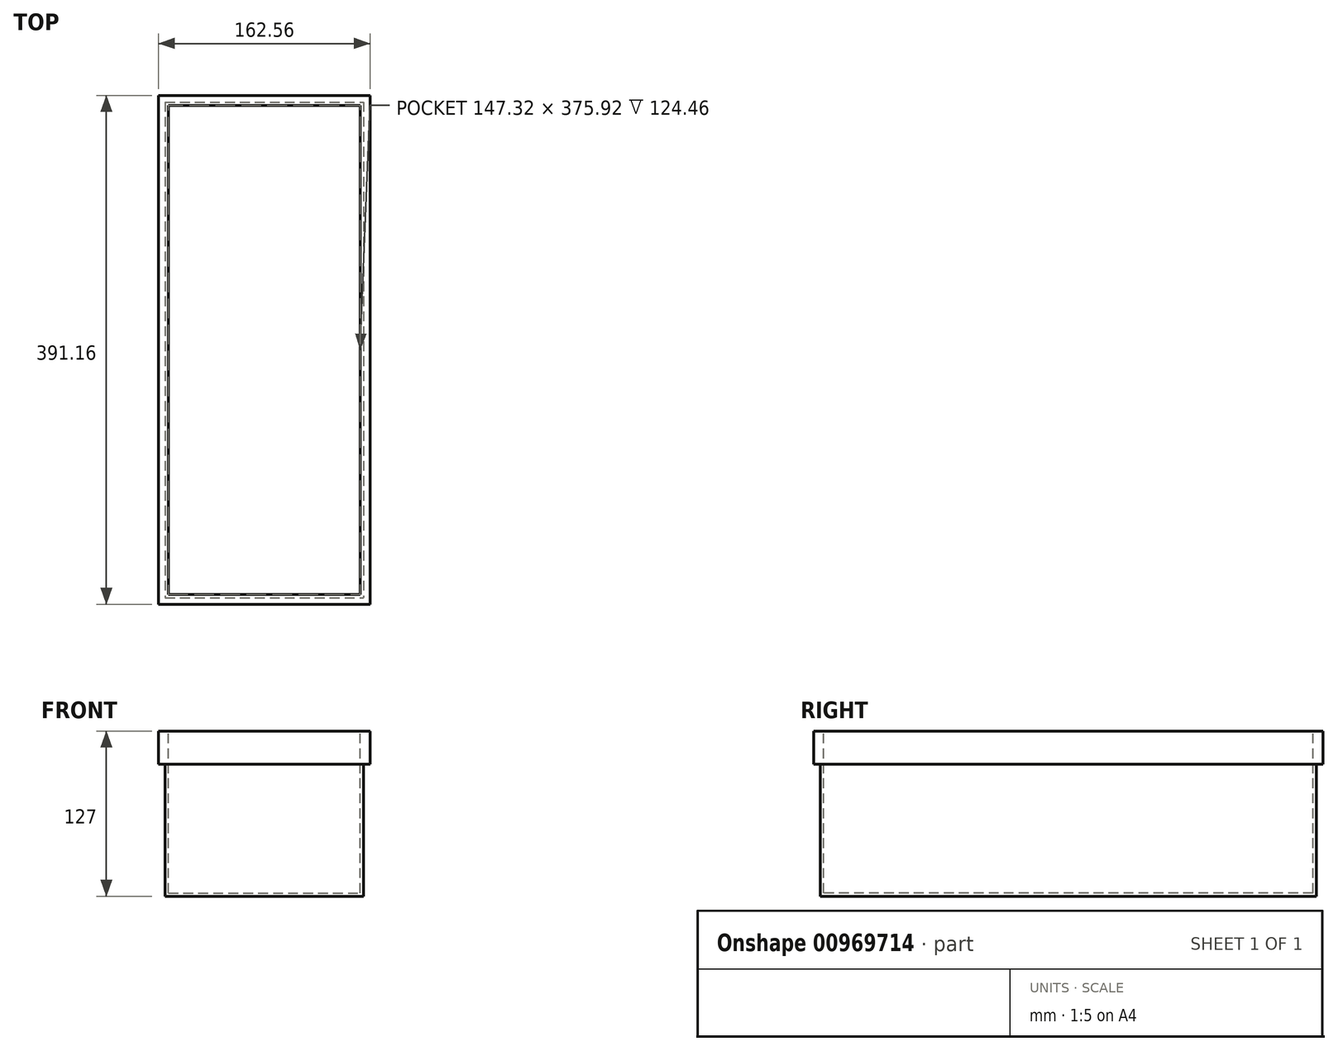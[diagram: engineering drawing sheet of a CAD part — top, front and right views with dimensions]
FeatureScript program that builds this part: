
annotation { "Feature Type Name" : "Feature", "Feature Type Description" : "" }
export const myFeature = defineFeature(function(context is Context, id is Id, definition is map)
    precondition{}
    {
        {
            var Q0;
            Q0=qCreatedBy(makeId("Front.planeOp"),FACE);
            var sketch = newSketch(context, id + "F0", { "sketchPlane" : qUnion([Q0])});
            skLineSegment(sketch, "E0.bottom", {"start": v(0, 0) * mm, "end": v(152.4, 0) * mm});
            skLineSegment(sketch, "E0.top", {"start": v(0, 127) * mm, "end": v(152.4, 127) * mm});
            skLineSegment(sketch, "E0.left", {"start": v(0, 0) * mm, "end": v(0, 127) * mm});
            skLineSegment(sketch, "E0.right", {"start": v(152.4, 0) * mm, "end": v(152.4, 127) * mm});
            skSolve(sketch);
        }
        {
            var Q0;
            Q0=makeQuery(id+"F0.imprint","IMPRINT",FACE,{"disambiguationData":[TD([[makeQuery(id+"F0.imprint","IMPRINT",EDGE,{"derivedFrom":sQuery(id+"F0.wireOp",EDGE,"E0.bottom")}),1.0]])]});
            extrude(context, id + "F1", {"entities" : qUnion([Q0]), "oppositeDirection" : true, "depth" : 381 * mm, "offsetDistance" : 25.4 * mm});
        }
        {
            var Q0;
            Q0=makeQuery(id+"F1.opExtrude","SWEPT_FACE",FACE,{"disambiguationData":[OSD([sQuery(id+"F0.wireOp",EDGE,"E0.top")])]});
            shell(context, id + "F2", {"entities" : qUnion([Q0]), "thickness" : 2.54 * mm});
        }
        {
            var Q0;
            Q0=makeQuery(id+"F1.opExtrude","SWEPT_FACE",FACE,{"disambiguationData":[OSD([sQuery(id+"F0.wireOp",EDGE,"E0.top")])]});
            var sketch = newSketch(context, id + "F3", { "sketchPlane" : qUnion([Q0])});
            skLineSegment(sketch, "E1.bottom", {"start": v(157.48, -5.08) * mm, "end": v(-5.08, -5.08) * mm});
            skLineSegment(sketch, "E1.top", {"start": v(157.48, 386.08) * mm, "end": v(-5.08, 386.08) * mm});
            skLineSegment(sketch, "E1.left", {"start": v(157.48, -5.08) * mm, "end": v(157.48, 386.08) * mm});
            skLineSegment(sketch, "E1.right", {"start": v(-5.08, -5.08) * mm, "end": v(-5.08, 386.08) * mm});
            skSolve(sketch);
        }
        {
            var Q0;
            Q0=makeQuery(id+"F3.imprint","IMPRINT",FACE,{"disambiguationData":[TD([[makeQuery(id+"F3.imprint","IMPRINT",EDGE,{"derivedFrom":sQuery(id+"F3.wireOp",EDGE,"E1.bottom")}),-1.0]])]});
            extrude(context, id + "F4", {"entities" : qUnion([Q0]), "operationType" : NewBodyOperationType.ADD, "oppositeDirection" : true, "depth" : 25.4 * mm, "offsetDistance" : 25.4 * mm});
        }
    });
